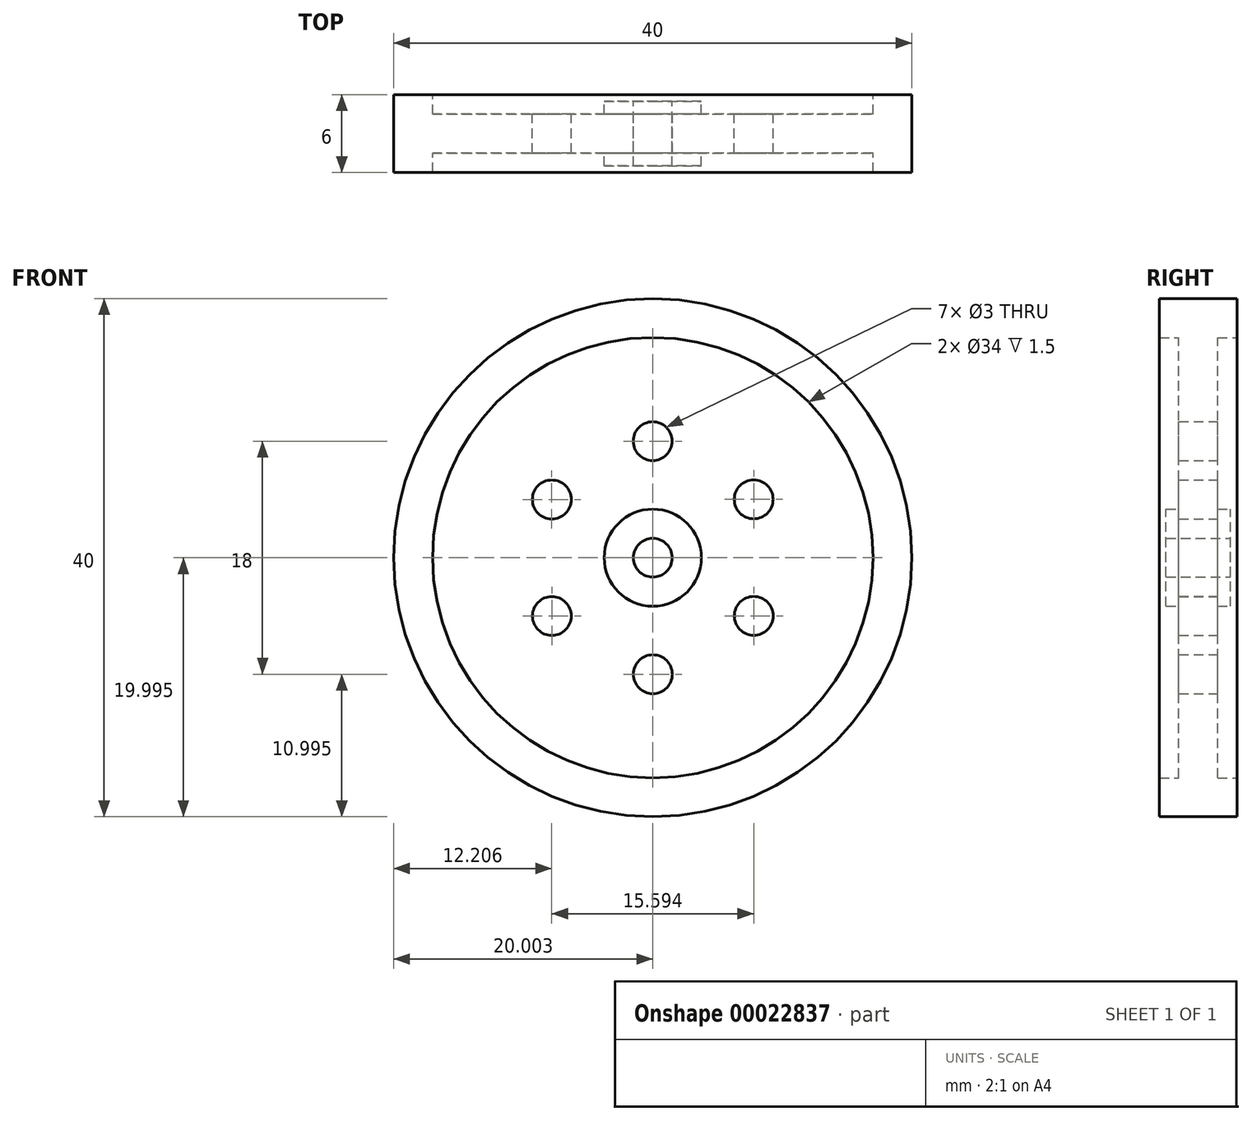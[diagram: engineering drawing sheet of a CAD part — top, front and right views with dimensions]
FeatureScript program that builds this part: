
annotation { "Feature Type Name" : "Feature", "Feature Type Description" : "" }
export const myFeature = defineFeature(function(context is Context, id is Id, definition is map)
    precondition{}
    {
        {
            var Q0;
            Q0=qCreatedBy(makeId("Front.planeOp"),FACE);
            var sketch = newSketch(context, id + "F0", { "sketchPlane" : qUnion([Q0])});
            skCircle(sketch, "E0", {"center": v(-104.43, 48.85) * mm, "radius": 20 * mm});
            skCircle(sketch, "E1", {"center": v(-104.43, 48.85) * mm, "radius": 1.5 * mm});
            skCircle(sketch, "E2", {"center": v(-104.43, 48.85) * mm, "radius": 3.75 * mm});
            skCircle(sketch, "E3", {"center": v(-104.43, 57.85) * mm, "radius": 1.5 * mm});
            skLineSegment(sketch, "E4", {"start": v(-104.43, 57.85) * mm, "end": v(-104.43, 48.85) * mm});
            skCircle(sketch, "E5.1.0", {"center": v(-112.22, 53.34) * mm, "radius": 1.5 * mm});
            skCircle(sketch, "E5.2.0", {"center": v(-112.22, 44.34) * mm, "radius": 1.5 * mm});
            skCircle(sketch, "E6.1.3.0", {"center": v(-104.42, 39.85) * mm, "radius": 1.5 * mm});
            skCircle(sketch, "E6.1.4.0", {"center": v(-96.63, 44.35) * mm, "radius": 1.5 * mm});
            skCircle(sketch, "E6.1.5.0", {"center": v(-96.64, 53.35) * mm, "radius": 1.5 * mm});
            skCircle(sketch, "E7", {"center": v(-104.43, 48.85) * mm, "radius": 17 * mm});
            skSolve(sketch);
        }
        {
            var Q0;
            Q0=makeQuery(id+"F0.imprint","IMPRINT",FACE,{"disambiguationData":[TD([[makeQuery(id+"F0.imprint","IMPRINT",EDGE,{"derivedFrom":sQuery(id+"F0.wireOp",EDGE,"E1")}),-1.0]])]});
            extrude(context, id + "F1", {"entities" : qUnion([Q0]), "endBound" : BoundingType.SYMMETRIC, "depth" : 5 * mm});
        }
        {
            var Q0;
            Q0=makeQuery(id+"F0.imprint","IMPRINT",FACE,{"disambiguationData":[TD([[makeQuery(id+"F0.imprint","IMPRINT",EDGE,{"derivedFrom":sQuery(id+"F0.wireOp",EDGE,"E2")}),-1.0]])]});
            extrude(context, id + "F2", {"entities" : qUnion([Q0]), "operationType" : NewBodyOperationType.ADD, "endBound" : BoundingType.SYMMETRIC, "depth" : 3 * mm});
        }
        {
            var Q0;
            Q0=makeQuery(id+"F0.imprint","IMPRINT",FACE,{"disambiguationData":[TD([[makeQuery(id+"F0.imprint","IMPRINT",EDGE,{"derivedFrom":sQuery(id+"F0.wireOp",EDGE,"E0")}),1.0]])]});
            extrude(context, id + "F3", {"entities" : qUnion([Q0]), "operationType" : NewBodyOperationType.ADD, "endBound" : BoundingType.SYMMETRIC, "depth" : 6 * mm});
        }
    });
